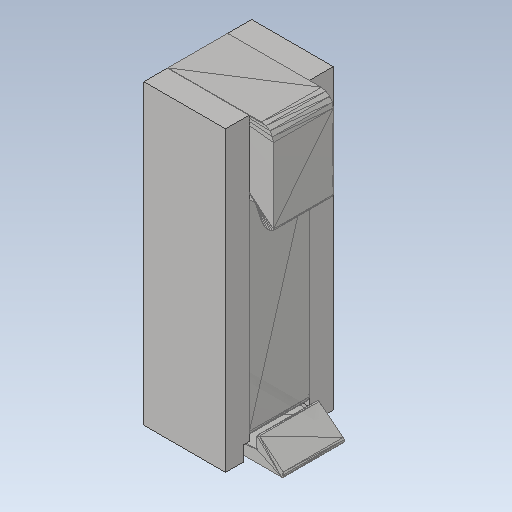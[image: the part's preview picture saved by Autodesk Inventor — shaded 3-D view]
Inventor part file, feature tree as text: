
AUTODESK INVENTOR PART (.ipt)
format: ipt  version: 2021 (Build 250183000, 183)  size: 146,432 bytes
history: native  units: mm
features: extrude x3, sketch x3, other x2
ambient origin geometry x8: Origin, YZ Plane, XZ Plane, XY Plane, X Axis, Y Axis, Z Axis, Center Point
bodies: Solid1 (feature_tree)
feature tree (8):
  other  "din_clip_01"
  extrude  "Extrusion1"  Depth=4.0mm TaperAngle=0.0deg
  extrude  "Extrusion2"  Depth=1.0mm
  extrude  "Extrusion3"  [1 undecoded]
  sketch  "Sketch1"  dims[d0=4.0mm d1=0.0mm d2=4.0mm d3=0.0mm]
  sketch  "Sketch2"  dims[d4=1.0mm d5=1.0mm]
  sketch  "Sketch3"  dims[d6=2.5mm d7=0.0mm]
  other  "MeshFeature2"
note: 1 required parameter value undecoded (feature->parameter linkage not recoverable at this tier; creation-order binding heuristic only, values carry confidence <= 0.55)
